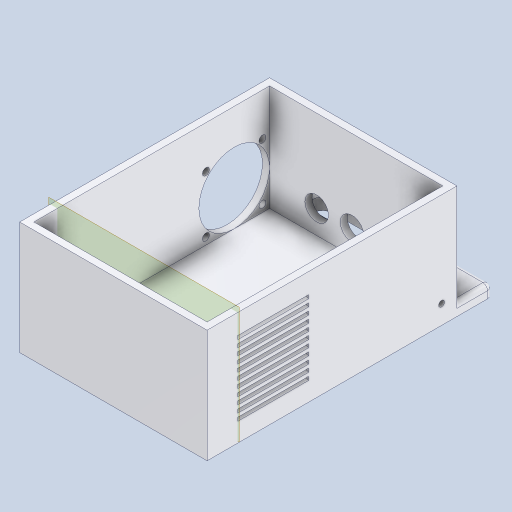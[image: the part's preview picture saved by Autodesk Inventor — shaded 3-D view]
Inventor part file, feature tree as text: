
AUTODESK INVENTOR PART (.ipt)
format: ipt  version: 2024 (Build 280153000, 153)  size: 466,432 bytes
history: native  units: mm
features: extrude x18, sketch x18, projected_geometry x15, fillet x1, plane x1
ambient origin geometry x8: Origin, YZ Plane, XZ Plane, XY Plane, X Axis, Y Axis, Z Axis, Center Point
bodies: Solid1 (feature_tree)
feature tree (53):
  extrude  "Extrusion1"  Depth=100.0mm
  extrude  "Extrusion2"  Depth=3.25mm
  extrude  "Extrusion3"  Depth=4.0mm
  extrude  "Extrusion4"  Depth=4.0mm
  extrude  "Extrusion5"  Depth=3.25mm
  extrude  "Extrusion6"  Depth=89.0mm
  extrude  "Extrusion7"  Depth=8.25mm
  extrude  "Extrusion8"  TaperAngle=0.0deg  [1 undecoded]
  sketch  "Sketch9"  dims[d17=7.5mm d18=0.0mm]
  extrude  "Extrusion10"  TaperAngle=0.0deg  [1 undecoded]
  extrude  "Extrusion11"  Depth=1.0mm TaperAngle=0.0deg
  extrude  "Extrusion12"  Depth=3.0mm
  extrude  "Extrusion13"  Depth=3.0mm TaperAngle=0.0deg
  extrude  "Extrusion14"  Depth=3.0mm
  extrude  "Extrusion15"  Depth=3.0mm
  extrude  "Extrusion16"  Depth=8.0mm
  extrude  "Extrusion17"  Depth=11.5mm
  fillet  "Fillet1"  Radius=47.5mm
  extrude  "Extrusion18"  Depth=8.0mm
  plane  "Work Plane2"
  extrude  "Extrusion19"  Depth=8.0mm
  sketch  "Sketch1"  dims[d0=51.5mm d1=100.0mm]
  sketch  "Sketch2"  dims[d2=3.25mm d3=3.25mm]
  projected_geometry  "Projected Loop1"
  sketch  "Sketch3"  dims[d4=4.0mm d5=4.0mm]
  projected_geometry  "Projected Loop2"
  sketch  "Sketch4"  dims[d6=4.0mm d7=11.5mm]
  projected_geometry  "Projected Loop3"
  sketch  "Sketch5"  dims[d8=1.0mm d9=0.0mm d10=3.25mm]
  sketch  "Sketch6"  dims[d11=52.0mm d12=89.0mm]
  sketch  "Sketch7"  dims[d13=2.25mm d14=8.25mm]
  projected_geometry  "Projected Loop4"
  sketch  "Sketch8"  dims[d15=8.25mm d16=0.0mm]
  projected_geometry  "Projected Loop5"
  projected_geometry  "Projected Loop6"
  sketch  "Sketch11"  dims[d19=0.0mm d20=1.0mm d21=0.0mm]
  projected_geometry  "Projected Loop9"
  sketch  "Sketch12"  dims[d22=3.0mm d23=3.0mm]
  projected_geometry  "Projected Loop10"
  sketch  "Sketch13"  dims[d24=3.0mm d26=3.0mm d27=0.0mm]
  projected_geometry  "Projected Loop11"
  sketch  "Sketch14"  dims[d28=3.0mm d29=3.0mm]
  projected_geometry  "Projected Loop12"
  sketch  "Sketch15"  dims[d30=3.0mm d31=3.0mm]
  projected_geometry  "Projected Loop13"
  sketch  "Sketch16"  dims[d32=45.0mm d33=0.0mm d34=8.0mm]
  projected_geometry  "Projected Loop14"
  sketch  "Sketch17"  dims[d35=3.25mm d36=11.5mm d37=47.5mm]
  projected_geometry  "Projected Loop15"
  sketch  "Sketch18"  dims[d39=8.0mm d42=74.0mm]
  sketch  "Sketch19"  dims[d43=5.0mm d44=0.0mm d45=8.0mm d46=1.5mm d47=0.0mm d48=3.0mm d49=30.0mm d50=30.0mm d51=0.0mm d52=0.0mm d53=30.0mm d54=24.0mm d55=3.0mm d56=12.0mm d57=3.0mm d58=24.0mm d59=24.0mm d60=24.0mm d61=3.0mm d62=3.0mm d63=30.0mm d64=0.0mm d65=0.0mm d66=3.0mm d67=0.0mm d68=10.0mm d69=10.0mm d70=10.0mm d71=10.0mm d72=10.0mm d73=10.0mm d74=10.0mm d75=10.0mm d90=12.0mm d91=0.0mm d92=10.0mm d93=0.0mm d95=10.0mm d96=10.0mm d97=0.0mm d100=14.0mm d101=2.5mm d104=5.0mm d105=0.0mm d106=0.0mm d108=3.5mm d109=10.0mm d110=0.0mm d112=3.5mm d113=7.5mm d114=10.0mm d124=15.0mm d129=10.0mm d131=20.0mm d132=10.0mm d133=0.0mm d134=4.2mm d135=4.2mm d136=4.2mm d137=5.0mm d138=0.0mm d139=5.0mm d140=15.0mm d141=0.0mm d142=8.35mm d143=8.35mm d144=15.0mm d145=15.0mm d146=0.0mm d147=15.0mm d148=0.0mm d149=2.0mm d150=10.0mm d151=0.0mm d152=10.0mm d153=5.0mm d154=30.0deg d155=1.5mm d156=1.5mm d157=130.0mm d159=3.0mm d160=10.0mm d162=10.0mm d164=30.0mm d165=0.0mm d76=0.5mm d77=0.872665mm d78=0.5mm d79=0.872665mm]
  projected_geometry  "Projected Loop16"
  projected_geometry  "Projected Loop17"
note: 2 required parameter values undecoded (feature->parameter linkage not recoverable at this tier; creation-order binding heuristic only, values carry confidence <= 0.55)
